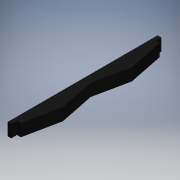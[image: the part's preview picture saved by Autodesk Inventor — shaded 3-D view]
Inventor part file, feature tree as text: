
AUTODESK INVENTOR PART (.ipt)
format: ipt  version: 2017 (Build 210142000, 142)  size: 118,784 bytes
history: native  units: in
note: dims shown in document units (in); Inventor stores cm internally (conversion verified against a paired STEP export)
features: extrude x3, sketch x3
ambient origin geometry x8: Origin, YZ Plane, XZ Plane, XY Plane, X Axis, Y Axis, Z Axis, Center Point
bodies: Solid1 (feature_tree)
feature tree (6):
  extrude  "Extrusion1"  Depth=0.134in
  sketch  "Sketch2"  dims[d2=0.134in d3=0.6115in]
  extrude  "Extrusion2"  Depth=0.134in
  extrude  "Extrusion3"  Depth=0.101in
  sketch  "Sketch1"  dims[d0=2.436in d1=0.134in]
  sketch  "Sketch3"  dims[d4=1.223in d5=0.6115in d6=0.125in d7=0.125in d8=0.2875in d9=0.0in d10=0.065in d11=0.065in d12=0.101in d13=0.0in d14=0.101in d15=0.0in]
